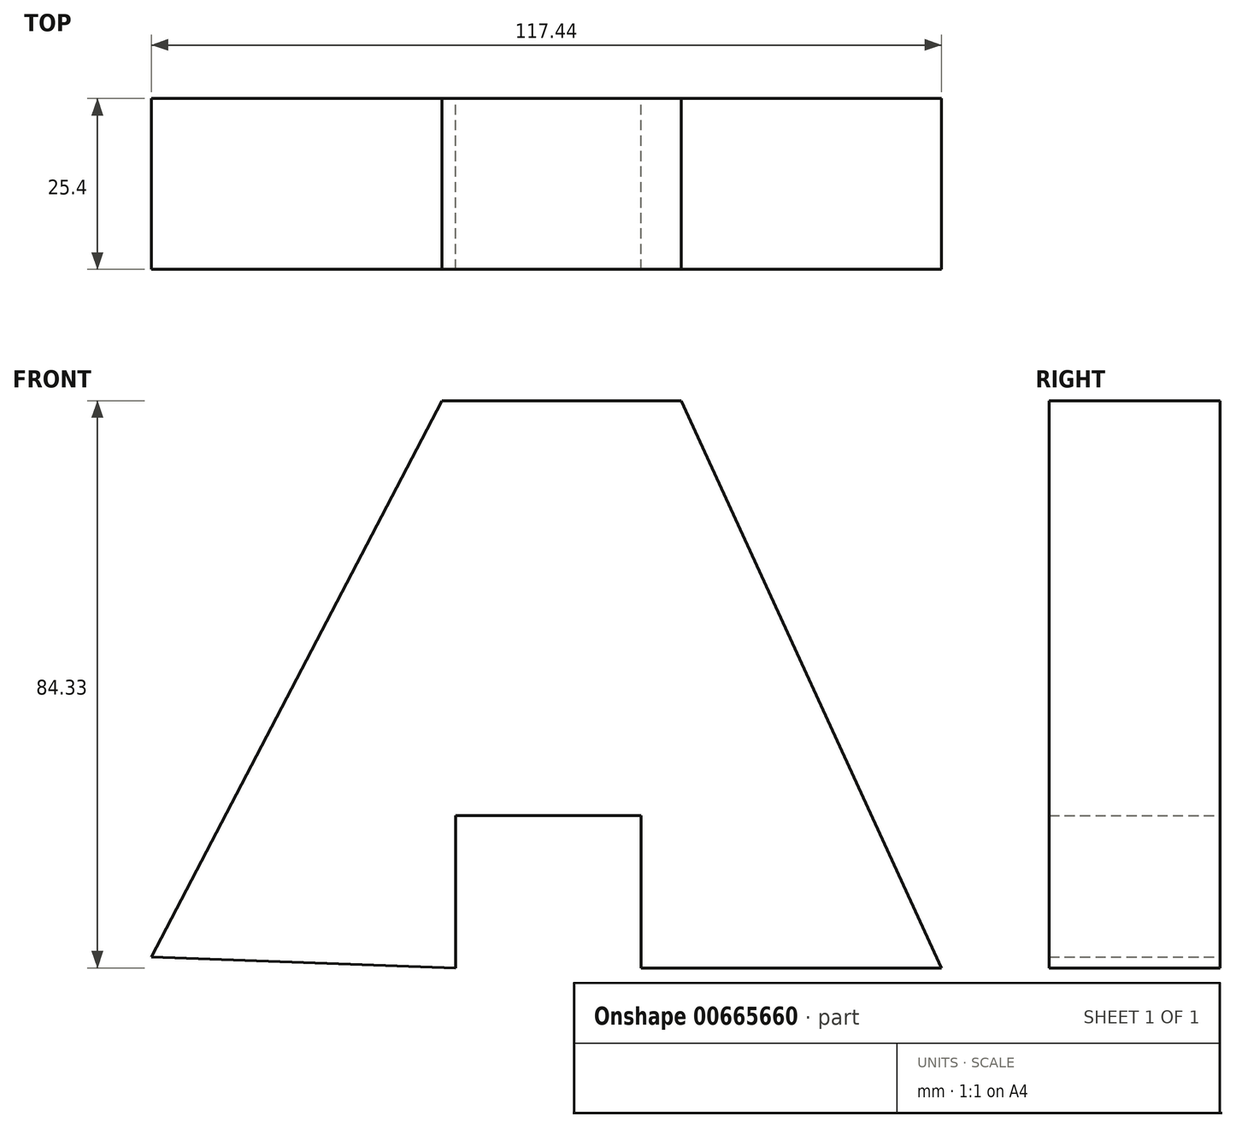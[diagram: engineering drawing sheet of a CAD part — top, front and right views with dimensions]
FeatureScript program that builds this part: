
annotation { "Feature Type Name" : "Feature", "Feature Type Description" : "" }
export const myFeature = defineFeature(function(context is Context, id is Id, definition is map)
    precondition{}
    {
        {
            var Q0;
            Q0=qCreatedBy(makeId("Front.planeOp"),FACE);
            var sketch = newSketch(context, id + "F0", { "sketchPlane" : qUnion([Q0])});
            skLineSegment(sketch, "E0", {"start": v(-57.9, -46.18) * mm, "end": v(-14.7, 36.5) * mm});
            skLineSegment(sketch, "E1", {"start": v(20.88, 36.5) * mm, "end": v(-14.7, 36.5) * mm});
            skLineSegment(sketch, "E2", {"start": v(20.88, 36.5) * mm, "end": v(59.54, -47.82) * mm});
            skLineSegment(sketch, "E3", {"start": v(59.54, -47.82) * mm, "end": v(14.91, -47.82) * mm});
            skLineSegment(sketch, "E4", {"start": v(14.91, -47.82) * mm, "end": v(14.91, -25.2) * mm});
            skLineSegment(sketch, "E5", {"start": v(14.91, -25.2) * mm, "end": v(-12.65, -25.2) * mm});
            skLineSegment(sketch, "E6", {"start": v(-12.65, -25.2) * mm, "end": v(-12.65, -47.82) * mm});
            skLineSegment(sketch, "E7", {"start": v(-12.65, -47.82) * mm, "end": v(-57.9, -46.18) * mm});
            skSolve(sketch);
        }
        {
            var Q0;
            Q0 = qSketchRegion(id + "F0", true);
            extrude(context, id + "F1", {"entities" : qUnion([Q0]), "depth" : 25.4 * mm, "offsetDistance" : 25.4 * mm});
        }
    });
